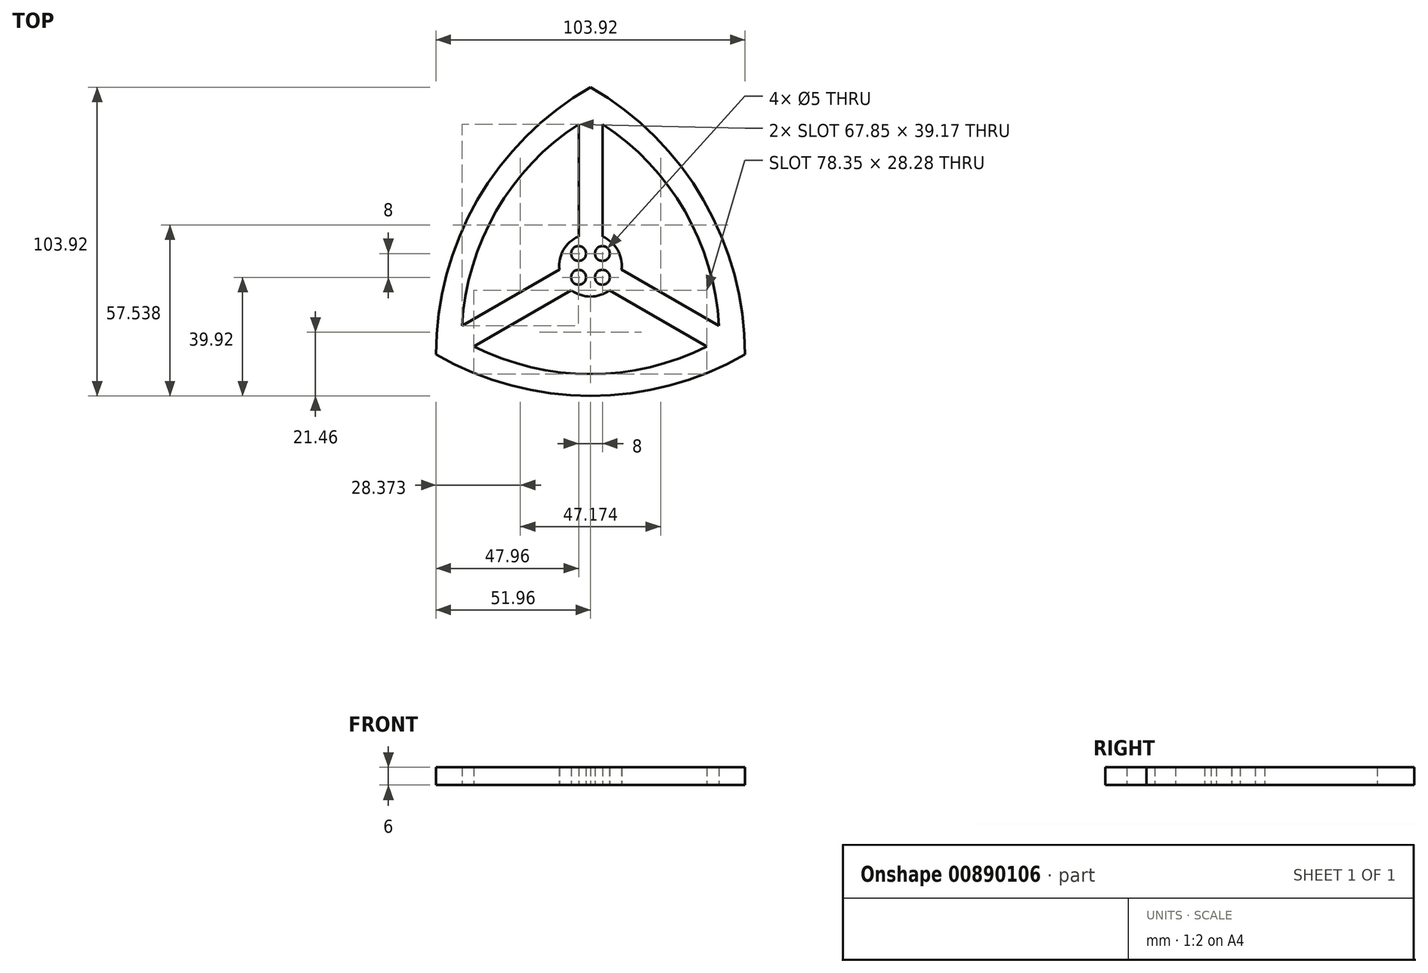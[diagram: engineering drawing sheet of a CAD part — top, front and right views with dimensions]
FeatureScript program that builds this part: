
annotation { "Feature Type Name" : "Feature", "Feature Type Description" : "" }
export const myFeature = defineFeature(function(context is Context, id is Id, definition is map)
    precondition{}
    {
        {
            var Q0;
            Q0=qCreatedBy(makeId("Top.planeOp"),FACE);
            var sketch = newSketch(context, id + "F0", { "sketchPlane" : qUnion([Q0])});
            skLineSegment(sketch, "E0", {"start": v(0, 0) * mm, "end": v(120, 0) * mm});
            skLineSegment(sketch, "E1", {"start": v(0.15, 0.03) * mm, "end": v(0.15, 120.03) * mm});
            skPoint(sketch, "E2.start.orphan", {"position": v(60, 0) * mm});
            skArc(sketch, "E3", {"start": v(8.04, 30) * mm, "mid": v(60, 16.08) * mm, "end": v(111.96, 30) * mm});
            skArc(sketch, "E4", {"start": v(60, 120) * mm, "mid": v(21.96, 81.96) * mm, "end": v(8.04, 30) * mm});
            skArc(sketch, "E5", {"start": v(111.96, 30) * mm, "mid": v(98.04, 81.96) * mm, "end": v(60, 120) * mm});
            skCircle(sketch, "E6", {"center": v(56, 64) * mm, "radius": 2.5 * mm});
            skCircle(sketch, "E7", {"center": v(64, 64) * mm, "radius": 2.5 * mm});
            skCircle(sketch, "E8", {"center": v(56, 56) * mm, "radius": 2.5 * mm});
            skCircle(sketch, "E9", {"center": v(64, 56) * mm, "radius": 2.5 * mm});
            skArc(sketch, "E10", {"start": v(53.6, 51.68) * mm, "mid": v(60, 49.5) * mm, "end": v(66.4, 51.68) * mm});
            skArc(sketch, "E11", {"start": v(103.17, 39.7) * mm, "mid": v(91.7, 78.3) * mm, "end": v(64, 107.54) * mm});
            skArc(sketch, "E12", {"start": v(20.83, 32.76) * mm, "mid": v(60, 23.4) * mm, "end": v(99.17, 32.76) * mm});
            skArc(sketch, "E13", {"start": v(56, 107.54) * mm, "mid": v(28.3, 78.3) * mm, "end": v(16.83, 39.7) * mm});
            skLineSegment(sketch, "E14", {"start": v(64, 85) * mm, "end": v(64, 107.54) * mm});
            skLineSegment(sketch, "E15", {"start": v(56, 85) * mm, "end": v(56, 107.54) * mm});
            skLineSegment(sketch, "E16", {"start": v(64, 85) * mm, "end": v(64, 69.7) * mm});
            skLineSegment(sketch, "E17", {"start": v(56, 85) * mm, "end": v(56, 69.7) * mm});
            skPoint(sketch, "E18.start.orphan", {"position": v(60, 85) * mm});
            skLineSegment(sketch, "E19", {"start": v(31.8, 48.34) * mm, "end": v(49.6, 58.6) * mm});
            skLineSegment(sketch, "E20", {"start": v(35.8, 41.41) * mm, "end": v(53.6, 51.68) * mm});
            skLineSegment(sketch, "E21", {"start": v(35.8, 41.41) * mm, "end": v(20.83, 32.76) * mm});
            skLineSegment(sketch, "E22", {"start": v(31.8, 48.34) * mm, "end": v(16.83, 39.7) * mm});
            skPoint(sketch, "E23.end.orphan", {"position": v(50.9, 54.75) * mm});
            skPoint(sketch, "E23.start.orphan", {"position": v(33.8, 44.87) * mm});
            skLineSegment(sketch, "E24", {"start": v(88.2, 48.34) * mm, "end": v(103.17, 39.7) * mm});
            skLineSegment(sketch, "E25", {"start": v(84.2, 41.41) * mm, "end": v(99.17, 32.76) * mm});
            skLineSegment(sketch, "E26", {"start": v(88.2, 48.34) * mm, "end": v(70.4, 58.6) * mm});
            skLineSegment(sketch, "E27", {"start": v(84.2, 41.41) * mm, "end": v(66.4, 51.68) * mm});
            skPoint(sketch, "E28.orphan", {"position": v(69.1, 54.75) * mm});
            skPoint(sketch, "E29.start.orphan", {"position": v(86.2, 44.88) * mm});
            skArc(sketch, "E30.trimOffspring", {"start": v(70.4, 58.6) * mm, "mid": v(69.1, 65.25) * mm, "end": v(64, 69.7) * mm});
            skArc(sketch, "E31.trimOffspring", {"start": v(56, 69.7) * mm, "mid": v(50.9, 65.25) * mm, "end": v(49.6, 58.6) * mm});
            skSolve(sketch);
        }
        {
            var Q0;
            Q0=makeQuery(id+"F0.imprint","IMPRINT",FACE,{"disambiguationData":[TD([[makeQuery(id+"F0.imprint","IMPRINT",EDGE,{"derivedFrom":sQuery(id+"F0.wireOp",EDGE,"E3")}),1.0]])]});
            extrude(context, id + "F1", {"entities" : qUnion([Q0]), "depth" : 6 * mm, "offsetDistance" : 25 * mm});
        }
    });
